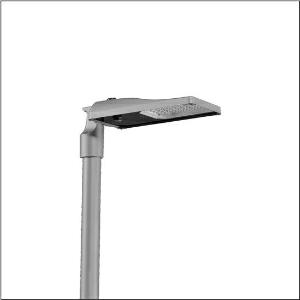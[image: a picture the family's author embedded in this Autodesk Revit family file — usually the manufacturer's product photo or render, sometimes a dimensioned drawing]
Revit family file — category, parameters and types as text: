
# Revit family: streetlight_sl_31_mini___p0_8a_5xh6u31t08ja_d345
name_source: partatom
category: Lighting Fixtures
units: mm (PartAtom-declared; Revit-internal decimal feet)

## family parameters
Cut with Voids When Loaded = No
Host = Face
Light Source = No
Part Type = Normal
Room Calculation Point = No
Round Connector Dimension = Use Diameter
Shared = No

## types (1)
- --- (1 x LED, 12370 lm, 82.5 W, 3000K)
    Apparent Load = 83 VA
    CIE Flux Codes = 36 69 97 100 100
    Color Rendering = 70
    Color Temperature = 3000K
    Default Elevation = 1800 mm
    Description = Streetlight SL 31 mini, mast luminaire, primary light control with lens, of PMMA, primary optical cover: cover, of toughened safety glass, transparent, light distribution: P0.8a, light emission: direct distribution, primary light characteristic: asymmetric, installation type: post-top, side-entry, LED, High Power LED, rated luminous flux: 12.370lm, luminous efficacy: 150lm/W, light colour: 730, colour temperature: 3000K, control: presetting dimming logarithmic, flexible luminous flux parameterisation, time-dependent luminous flux control, constant luminous flux control, power reduction, intelligent temperature release in ECG and LED module, overheat protection, with cable H07RN-F 2x 1.5mm², mains connection: 220..240V, AC, 50/60Hz, connection cable pre-assembled, cable length: 10,5m, start of lifetime: 83W, end of service life: 90W, reduction: 37W, luminaire housing, of diecast aluminium, powder-coated, Siteco® metallic grey (DB 702S), corrosivity category C5 high according to DIN EN ISO 12944, sealing non-destructively replaceable, multi-level sealing system, mast flange (76/60mm) included as standard, inclination: -15°..+20° (post-top) | -20°..+20° (side-entry), adjustable in 5° steps, no sealing on luminaire upper side, Smart Interface below and above, protection rating (complete): IP66, insulation class (complete): insulation class II (safety insulation), certification: CE, ENEC, ENEC+, VDE, UKCA, ZD4i, impact resistance: IK09, permissible operating ambient temperature for outdoor applications: -40..+50°C, standard-compliant lighting for roads and squares, packaging unit: 1 piece

Light Distribution: P0.8a
    Height = 76 mm
    Lamp = 1 x LED
    Lamp Light Flux = 12370 lm
    Lamp Power = 82.5 W
    Lamp count = 1
    Length = 547 mm
    Luminous efficacy = 150 lm/W
    Manufacturer = Siteco
    ModVariant = No
    Model = 5XH6U31T08JA
    Number of Poles = 1
    OnlyDefault = Yes
    Power Factor = 1
    Product Name = Streetlight SL 31 mini | P0.8a
    Product group = mast luminaire | pylon top
    ProductGroupID = 6100
    Protection Class = Protection class II
    Protection Degree = IP 66
    RLX_Detail_Level = 1
    RLX_Emergency_Light_Flux = 0 lm
    RLX_Emergency_Type = 0
    RLX_Emergency_Type_DB = No
    RlxData = <blob elided: 39917 chars, md5=c3bf661d>
    Socket = socket
    Standby Power = 0 W
    System Light Flux = 12370 lm
    System Power = 83 W
    Type Comments = factory setting: luminous flux: 100 % | dim-lin: 254 | 870 mA
    Type Image = l_1300332.jpg
    URL = http://relux.com
    VarID = @adj_018173
    Voltage = 0 V
    Weight = 0.00 kg
    Width = 265 mm

## geometry (parser evidence)
native form markers: Blend x4, Sweep x9
no freeform markers — native parametric forms only
